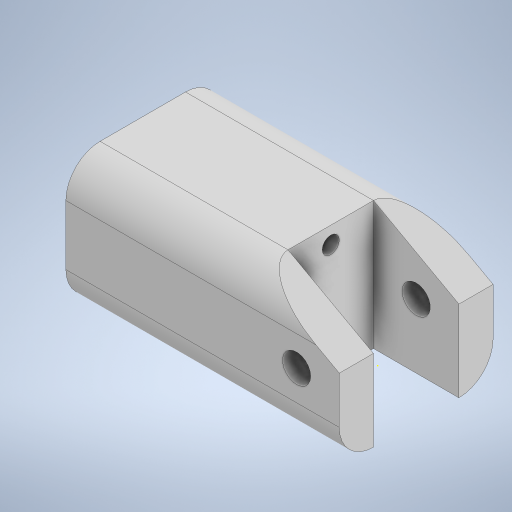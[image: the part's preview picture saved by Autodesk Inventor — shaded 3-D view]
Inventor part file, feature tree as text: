
AUTODESK INVENTOR PART (.ipt)
format: ipt  version: 2024 (Build 280153000, 153)  size: 457,728 bytes
history: native  units: mm
features: sketch x24, extrude x21, chamfer x3, move_body x3, plane x2, split x2, boolean_combine x1, fillet x1
ambient origin geometry x8: Origin, YZ Plane, XZ Plane, XY Plane, X Axis, Y Axis, Z Axis, Center Point
bodies: Solid1 (feature_tree), Solid2 (feature_tree), Solid3 (feature_tree), Solid4 (feature_tree), Solid5 (feature_tree)
feature tree (57):
  extrude  "Extrusion1"  Depth=16.0mm
  sketch  "Sketch2"  dims[d2=15.0mm d3=0.0mm d4=10.0mm]
  extrude  "Extrusion2"  Depth=10.0mm
  chamfer  "Chamfer1"  Distance=21.25mm
  extrude  "Extrusion3"  Depth=10.0mm TaperAngle=0.0deg
  extrude  "Extrusion4"  Depth=11.5mm TaperAngle=0.0deg
  extrude  "Extrusion5"  Depth=1.0mm TaperAngle=0.0deg
  chamfer  "Chamfer2"  Distance=6.0mm Angle=45.0deg
  sketch  "Sketch6"  dims[d14=7.0mm d15=11.5mm d16=0.0mm]
  extrude  "Extrusion6"  Depth=15.0mm
  extrude  "Extrusion7"  Depth=45.25mm TaperAngle=0.0deg
  chamfer  "Chamfer3"  Distance=11.5mm Angle=45.0deg
  sketch  "Sketch9"  dims[d26=3.3mm d27=45.25mm d28=0.0mm d29=11.5mm d30=5.5mm d31=45.0deg]
  extrude  "Extrusion8"  Depth=65.75mm TaperAngle=0.0deg
  extrude  "Extrusion9"  Depth=9.0mm TaperAngle=0.0deg
  extrude  "Extrusion10"  Depth=13.0mm TaperAngle=0.0deg
  sketch  "Sketch13"  dims[d43=24.0mm d44=21.0mm d45=0.0mm]
  extrude  "Extrusion11"  Depth=21.0mm TaperAngle=0.0deg
  extrude  "Extrusion12"  TaperAngle=0.0deg  [1 undecoded]
  extrude  "Extrusion13"  Depth=6.0mm TaperAngle=0.0deg
  plane  "Work Plane1"
  split  "Split1"
  move_body  "Move Body1"
  extrude  "Extrusion14"  Depth=10.0mm TaperAngle=0.0deg
  move_body  "Move Body2"
  extrude  "Extrusion15"  TaperAngle=0.0deg  [1 undecoded]
  plane  "Work Plane2"
  split  "Split2"
  move_body  "Move Body3"
  boolean_combine  "Combine1"
  extrude  "Extrusion16"  Depth=0.5mm TaperAngle=0.0deg
  extrude  "Extrusion17"  Depth=10.0mm TaperAngle=0.0deg
  extrude  "Extrusion19"  Depth=1.0mm TaperAngle=0.0deg
  extrude  "Extrusion20"  Depth=4.0mm
  sketch  "Sketch24"
  sketch  "Sketch25"
  extrude  "Extrusion23"  [1 undecoded]
  extrude  "Extrusion24"  [1 undecoded]
  fillet  "Fillet4"  [1 undecoded]
  sketch  "Sketch1"  dims[d0=36.0mm d1=16.0mm]
  sketch  "Sketch3"  dims[d5=10.0mm]
  sketch  "Sketch4"  dims[d6=3.3mm d7=21.25mm d8=0.0mm]
  sketch  "Sketch5"  dims[d9=10.0mm d10=5.5mm d11=45.0deg d12=10.0mm d13=0.0mm]
  sketch  "Sketch7"  dims[d17=3.3mm d18=1.0mm d19=0.0mm d20=6.0mm d21=11.5mm d22=45.0deg]
  sketch  "Sketch8"  dims[d23=15.0mm d24=0.0mm d25=9.0mm]
  sketch  "Sketch10"  dims[d32=2.0mm d33=65.75mm d34=0.0mm]
  sketch  "Sketch11"  dims[d35=0.5mm d36=0.0mm d37=9.0mm d38=0.0mm]
  sketch  "Sketch12"  dims[d39=0.5mm d40=0.0mm d41=13.0mm d42=0.0mm]
  sketch  "Sketch14"  dims[d46=12.25mm d47=-12.0mm d48=0.0mm d49=0.0mm]
  sketch  "Sketch15"  dims[d50=30.0mm d51=0.0mm d52=6.0mm d53=0.0mm d54=0.0mm]
  sketch  "Sketch16"  dims[d56=10.0mm d57=20.0mm d58=0.0mm]
  sketch  "Sketch17"  dims[d59=3.75mm d60=-10.0mm d61=0.0mm d62=0.0mm]
  sketch  "Sketch18"  dims[d64=0.5mm d65=0.0mm d66=0.5mm d67=0.0mm]
  sketch  "Sketch19"  dims[d71=3.0mm d72=10.0mm d73=0.0mm]
  sketch  "Sketch20"  dims[d74=10.0mm d75=0.0mm d81=1.0mm d82=0.0mm]
  sketch  "Sketch22"  dims[d83=1.0mm d84=0.0mm d85=4.0mm]
  sketch  "Sketch23"  dims[d63=0.0mm]
note: 5 required parameter values undecoded (feature->parameter linkage not recoverable at this tier; creation-order binding heuristic only, values carry confidence <= 0.55)
